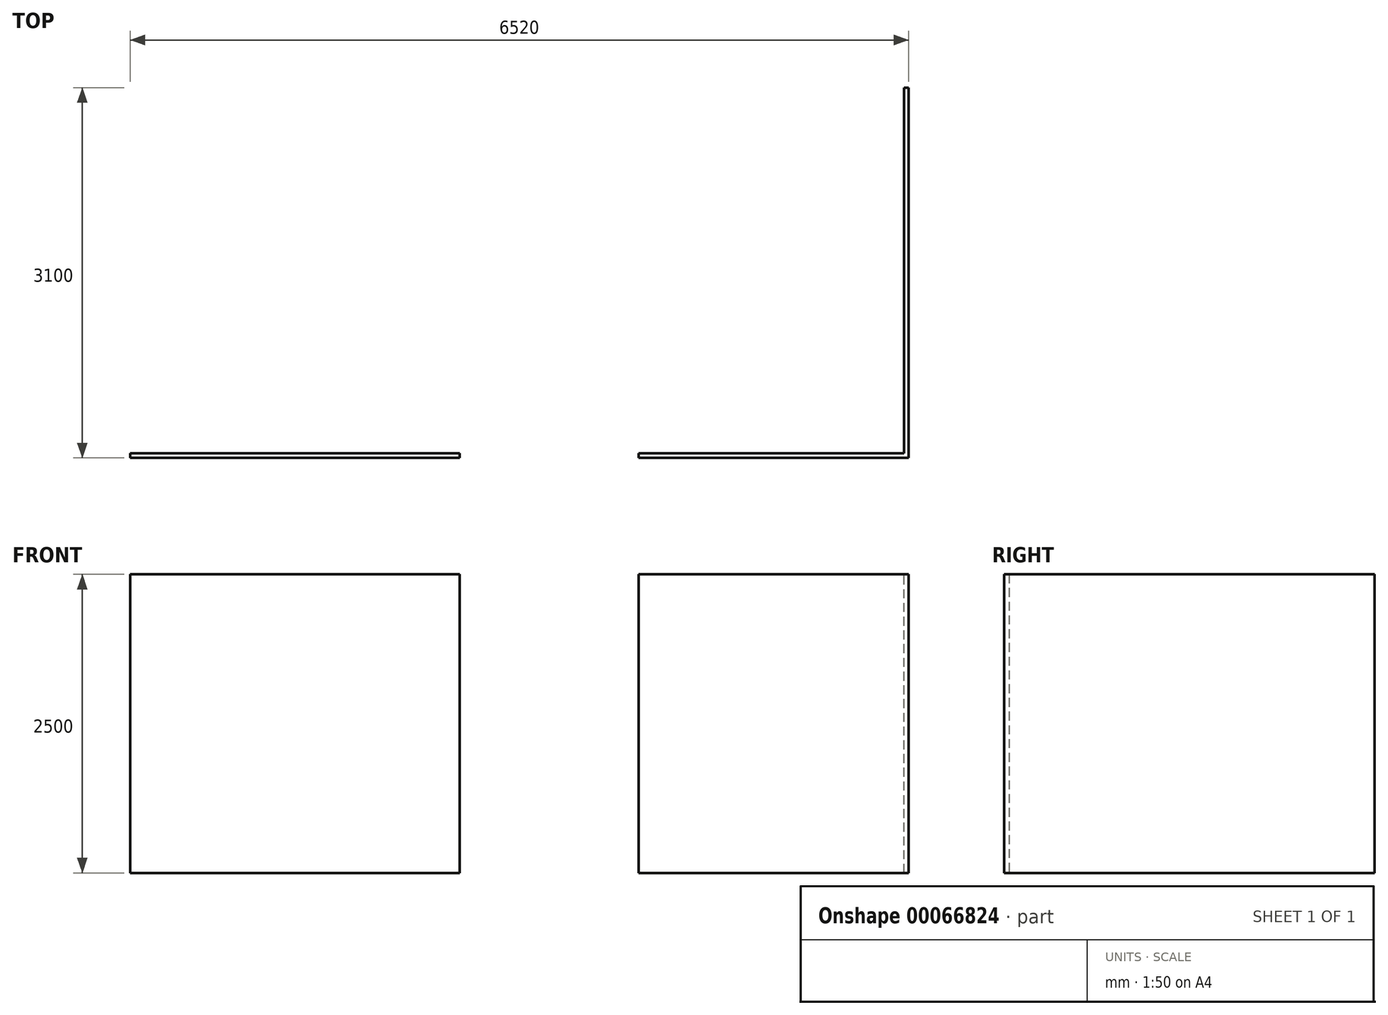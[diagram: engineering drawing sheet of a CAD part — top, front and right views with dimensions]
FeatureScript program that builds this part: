
annotation { "Feature Type Name" : "Feature", "Feature Type Description" : "" }
export const myFeature = defineFeature(function(context is Context, id is Id, definition is map)
    precondition{}
    {
        {
            var Q0;
            Q0=qCreatedBy(makeId("Front.planeOp"),FACE);
            var sketch = newSketch(context, id + "F0", { "sketchPlane" : qUnion([Q0])});
            skLineSegment(sketch, "E0.bottom", {"start": v(-1149.97, 1738.25) * mm, "end": v(1110.03, 1738.25) * mm});
            skLineSegment(sketch, "E0.top", {"start": v(-1149.97, -761.75) * mm, "end": v(1110.03, -761.75) * mm});
            skLineSegment(sketch, "E0.left", {"start": v(-1149.97, 1738.25) * mm, "end": v(-1149.97, -761.75) * mm});
            skLineSegment(sketch, "E0.right", {"start": v(1110.03, 1738.25) * mm, "end": v(1110.03, -761.75) * mm});
            skSolve(sketch);
        }
        {
            var Q0;
            Q0=makeQuery(id+"F0.imprint","IMPRINT",FACE,{"disambiguationData":[TD([[makeQuery(id+"F0.imprint","IMPRINT",EDGE,{"derivedFrom":sQuery(id+"F0.wireOp",EDGE,"E0.bottom")}),-1.0]])]});
            extrude(context, id + "F1", {"entities" : qUnion([Q0]), "depth" : 40 * mm});
        }
        {
            var Q0;
            Q0=makeQuery(id+"F1.opExtrude","SWEPT_FACE",FACE,{"disambiguationData":[OSD([sQuery(id+"F0.wireOp",EDGE,"E0.right")])]});
            var sketch = newSketch(context, id + "F2", { "sketchPlane" : qUnion([Q0])});
            skLineSegment(sketch, "E1.bottom", {"start": v(-40, 1738.25) * mm, "end": v(3060, 1738.25) * mm});
            skLineSegment(sketch, "E1.top", {"start": v(-40, -761.75) * mm, "end": v(3060, -761.75) * mm});
            skLineSegment(sketch, "E1.left", {"start": v(-40, 1738.25) * mm, "end": v(-40, -761.75) * mm});
            skLineSegment(sketch, "E1.right", {"start": v(3060, 1738.25) * mm, "end": v(3060, -761.75) * mm});
            skSolve(sketch);
        }
        {
            var Q0;
            {var subQ2=sQuery(id+"F2.wireOp",EDGE,"E1.left");Q0=makeQuery(id+"F2.imprint","IMPRINT",FACE,{"disambiguationData":[TD([[makeQuery(id+"F2.imprint","IMPRINT",EDGE,{"derivedFrom":subQ2}),1.0]])]});}
            var Q1;
            {var subQ2=sQuery(id+"F2.wireOp",EDGE,"E1.right");Q1=makeQuery(id+"F2.imprint","IMPRINT",FACE,{"disambiguationData":[TD([[makeQuery(id+"F2.imprint","IMPRINT",EDGE,{"derivedFrom":subQ2}),-1.0]])]});}
            extrude(context, id + "F3", {"entities" : qUnion([Q0, Q1]), "operationType" : NewBodyOperationType.ADD, "oppositeDirection" : true, "depth" : 40 * mm});
        }
        {
            var Q0;
            Q0=makeQuery(id+"F1.opExtrude","CAP_FACE",FACE,{"disambiguationData":[OSD([sQuery(id+"F0.wireOp",EDGE,"E0.bottom"),sQuery(id+"F0.wireOp",EDGE,"E0.top"),sQuery(id+"F0.wireOp",EDGE,"E0.left"),sQuery(id+"F0.wireOp",EDGE,"E0.right")])],"isStart":false});
            var sketch = newSketch(context, id + "F4", { "sketchPlane" : qUnion([Q0])});
            skLineSegment(sketch, "E2.bottom", {"start": v(-1149.97, 1738.25) * mm, "end": v(1110.03, 1738.25) * mm});
            skLineSegment(sketch, "E2.top", {"start": v(-1149.97, 1438.25) * mm, "end": v(810.03, 1438.25) * mm});
            skLineSegment(sketch, "E2.left", {"start": v(-1149.97, 1738.25) * mm, "end": v(-1149.97, 1438.25) * mm});
            skLineSegment(sketch, "E2.right", {"start": v(1110.03, 1738.25) * mm, "end": v(1110.03, 1438.25) * mm});
            skLineSegment(sketch, "E3.bottom", {"start": v(1110.03, -761.75) * mm, "end": v(810.03, -761.75) * mm});
            skLineSegment(sketch, "E3.left", {"start": v(1110.03, -761.75) * mm, "end": v(1110.03, 1438.25) * mm});
            skLineSegment(sketch, "E3.right", {"start": v(810.03, -761.75) * mm, "end": v(810.03, 1438.25) * mm});
            skLineSegment(sketch, "E4", {"start": v(750.03, 1438.25) * mm, "end": v(750.03, -761.75) * mm});
            skLineSegment(sketch, "E5", {"start": v(735.03, 1438.25) * mm, "end": v(735.03, -761.75) * mm});
            skLineSegment(sketch, "E6", {"start": v(675.03, 1438.25) * mm, "end": v(675.03, -761.75) * mm});
            skLineSegment(sketch, "E7", {"start": v(660.03, 1438.25) * mm, "end": v(660.03, -761.75) * mm});
            skLineSegment(sketch, "E8", {"start": v(600.03, 1438.25) * mm, "end": v(600.03, -761.75) * mm});
            skLineSegment(sketch, "E9", {"start": v(585.03, 1438.25) * mm, "end": v(585.03, -761.75) * mm});
            skLineSegment(sketch, "E10.1.0.0", {"start": v(360.03, 1438.25) * mm, "end": v(360.03, -761.75) * mm});
            skLineSegment(sketch, "E10.1.0.1", {"start": v(375.03, 1438.25) * mm, "end": v(375.03, -761.75) * mm});
            skLineSegment(sketch, "E10.1.0.2", {"start": v(435.03, 1438.25) * mm, "end": v(435.03, -761.75) * mm});
            skLineSegment(sketch, "E10.1.0.3", {"start": v(450.03, 1438.25) * mm, "end": v(450.03, -761.75) * mm});
            skLineSegment(sketch, "E10.1.0.4", {"start": v(510.03, 1438.25) * mm, "end": v(510.03, -761.75) * mm});
            skLineSegment(sketch, "E10.1.0.5", {"start": v(525.03, 1438.25) * mm, "end": v(525.03, -761.75) * mm});
            skLineSegment(sketch, "E10.2.0.0", {"start": v(135.03, 1438.25) * mm, "end": v(135.03, -761.75) * mm});
            skLineSegment(sketch, "E10.2.0.1", {"start": v(150.03, 1438.25) * mm, "end": v(150.03, -761.75) * mm});
            skLineSegment(sketch, "E10.2.0.2", {"start": v(210.03, 1438.25) * mm, "end": v(210.03, -761.75) * mm});
            skLineSegment(sketch, "E10.2.0.3", {"start": v(225.03, 1438.25) * mm, "end": v(225.03, -761.75) * mm});
            skLineSegment(sketch, "E10.2.0.4", {"start": v(285.03, 1438.25) * mm, "end": v(285.03, -761.75) * mm});
            skLineSegment(sketch, "E10.2.0.5", {"start": v(300.03, 1438.25) * mm, "end": v(300.03, -761.75) * mm});
            skLineSegment(sketch, "E10.3.0.0", {"start": v(-89.97, 1438.25) * mm, "end": v(-89.97, -761.75) * mm});
            skLineSegment(sketch, "E10.3.0.1", {"start": v(-74.97, 1438.25) * mm, "end": v(-74.97, -761.75) * mm});
            skLineSegment(sketch, "E10.3.0.2", {"start": v(-14.97, 1438.25) * mm, "end": v(-14.97, -761.75) * mm});
            skLineSegment(sketch, "E10.3.0.3", {"start": v(0.03, 1438.25) * mm, "end": v(0.03, -761.75) * mm});
            skLineSegment(sketch, "E10.3.0.4", {"start": v(60.03, 1438.25) * mm, "end": v(60.03, -761.75) * mm});
            skLineSegment(sketch, "E10.3.0.5", {"start": v(75.03, 1438.25) * mm, "end": v(75.03, -761.75) * mm});
            skLineSegment(sketch, "E10.4.0.0", {"start": v(-314.97, 1438.25) * mm, "end": v(-314.97, -761.75) * mm});
            skLineSegment(sketch, "E10.4.0.1", {"start": v(-299.97, 1438.25) * mm, "end": v(-299.97, -761.75) * mm});
            skLineSegment(sketch, "E10.4.0.2", {"start": v(-239.97, 1438.25) * mm, "end": v(-239.97, -761.75) * mm});
            skLineSegment(sketch, "E10.4.0.3", {"start": v(-224.97, 1438.25) * mm, "end": v(-224.97, -761.75) * mm});
            skLineSegment(sketch, "E10.4.0.4", {"start": v(-164.97, 1438.25) * mm, "end": v(-164.97, -761.75) * mm});
            skLineSegment(sketch, "E10.4.0.5", {"start": v(-149.97, 1438.25) * mm, "end": v(-149.97, -761.75) * mm});
            skLineSegment(sketch, "E10.5.0.0", {"start": v(-539.97, 1438.25) * mm, "end": v(-539.97, -761.75) * mm});
            skLineSegment(sketch, "E10.5.0.1", {"start": v(-524.97, 1438.25) * mm, "end": v(-524.97, -761.75) * mm});
            skLineSegment(sketch, "E10.5.0.2", {"start": v(-464.97, 1438.25) * mm, "end": v(-464.97, -761.75) * mm});
            skLineSegment(sketch, "E10.5.0.3", {"start": v(-449.97, 1438.25) * mm, "end": v(-449.97, -761.75) * mm});
            skLineSegment(sketch, "E10.5.0.4", {"start": v(-389.97, 1438.25) * mm, "end": v(-389.97, -761.75) * mm});
            skLineSegment(sketch, "E10.5.0.5", {"start": v(-374.97, 1438.25) * mm, "end": v(-374.97, -761.75) * mm});
            skLineSegment(sketch, "E10.6.0.0", {"start": v(-764.97, 1438.25) * mm, "end": v(-764.97, -761.75) * mm});
            skLineSegment(sketch, "E10.6.0.1", {"start": v(-749.97, 1438.25) * mm, "end": v(-749.97, -761.75) * mm});
            skLineSegment(sketch, "E10.6.0.2", {"start": v(-689.97, 1438.25) * mm, "end": v(-689.97, -761.75) * mm});
            skLineSegment(sketch, "E10.6.0.3", {"start": v(-674.97, 1438.25) * mm, "end": v(-674.97, -761.75) * mm});
            skLineSegment(sketch, "E10.6.0.4", {"start": v(-614.97, 1438.25) * mm, "end": v(-614.97, -761.75) * mm});
            skLineSegment(sketch, "E10.6.0.5", {"start": v(-599.97, 1438.25) * mm, "end": v(-599.97, -761.75) * mm});
            skLineSegment(sketch, "E10.7.0.0", {"start": v(-989.97, 1438.25) * mm, "end": v(-989.97, -761.75) * mm});
            skLineSegment(sketch, "E10.7.0.1", {"start": v(-974.97, 1438.25) * mm, "end": v(-974.97, -761.75) * mm});
            skLineSegment(sketch, "E10.7.0.2", {"start": v(-914.97, 1438.25) * mm, "end": v(-914.97, -761.75) * mm});
            skLineSegment(sketch, "E10.7.0.3", {"start": v(-899.97, 1438.25) * mm, "end": v(-899.97, -761.75) * mm});
            skLineSegment(sketch, "E10.7.0.4", {"start": v(-839.97, 1438.25) * mm, "end": v(-839.97, -761.75) * mm});
            skLineSegment(sketch, "E10.7.0.5", {"start": v(-824.97, 1438.25) * mm, "end": v(-824.97, -761.75) * mm});
            skLineSegment(sketch, "E10.8.0.2", {"start": v(-1139.97, 1438.25) * mm, "end": v(-1139.97, -761.75) * mm});
            skLineSegment(sketch, "E10.8.0.3", {"start": v(-1124.97, 1438.25) * mm, "end": v(-1124.97, -761.75) * mm});
            skLineSegment(sketch, "E10.8.0.4", {"start": v(-1064.97, 1438.25) * mm, "end": v(-1064.97, -761.75) * mm});
            skLineSegment(sketch, "E10.8.0.5", {"start": v(-1049.97, 1438.25) * mm, "end": v(-1049.97, -761.75) * mm});
            skLineSegment(sketch, "E10.direction1", {"start": v(585.03, -761.75) * mm, "end": v(360.03, -761.75) * mm, "construction": true});
            skPoint(sketch, "E11.end.orphan", {"position": v(585.03, 996.16) * mm});
            skPoint(sketch, "E12.end.orphan", {"position": v(600.03, 996.16) * mm});
            skPoint(sketch, "E13.end.orphan", {"position": v(660.03, 996.16) * mm});
            skPoint(sketch, "E14.end.orphan", {"position": v(675.03, 996.16) * mm});
            skPoint(sketch, "E15.end.orphan", {"position": v(750.03, 808.78) * mm});
            skPoint(sketch, "E16.end.orphan", {"position": v(735.03, 370.6) * mm});
            skSolve(sketch);
        }
        {
            var Q0;
            Q0=makeQuery(id+"F3.boolean.opBoolean","MERGE",FACE,{"derivedFrom":[makeQuery(id+"F1.opExtrude","SWEPT_FACE",FACE,{"disambiguationData":[OSD([sQuery(id+"F0.wireOp",EDGE,"E0.right")])]}),makeQuery(id+"F3.opExtrude","CAP_FACE",FACE,{"disambiguationData":[OSD([sQuery(id+"F2.wireOp",EDGE,"E1.bottom"),sQuery(id+"F2.wireOp",EDGE,"E1.top"),sQuery(id+"F2.wireOp",EDGE,"E1.left"),sQuery(id+"F2.wireOp",EDGE,"E1.right")])],"isStart":true})]});
            var sketch = newSketch(context, id + "F5", { "sketchPlane" : qUnion([Q0])});
            skLineSegment(sketch, "E17.bottom", {"start": v(-40, 1738.25) * mm, "end": v(3060, 1738.25) * mm});
            skLineSegment(sketch, "E17.top", {"start": v(260, 1438.25) * mm, "end": v(3060, 1438.25) * mm});
            skLineSegment(sketch, "E17.left", {"start": v(-40, 1738.25) * mm, "end": v(-40, 1438.25) * mm});
            skLineSegment(sketch, "E17.right", {"start": v(3060, 1738.25) * mm, "end": v(3060, 1438.25) * mm});
            skLineSegment(sketch, "E18.top", {"start": v(-40, -761.75) * mm, "end": v(260, -761.75) * mm});
            skLineSegment(sketch, "E18.left", {"start": v(-40, 1438.25) * mm, "end": v(-40, -761.75) * mm});
            skLineSegment(sketch, "E18.right", {"start": v(260, 1438.25) * mm, "end": v(260, -761.75) * mm});
            skLineSegment(sketch, "E19", {"start": v(260, 1087.29) * mm, "end": v(320, 1087.29) * mm});
            skLineSegment(sketch, "E20", {"start": v(320, 1438.25) * mm, "end": v(320, -761.75) * mm});
            skLineSegment(sketch, "E21", {"start": v(320, 1087.29) * mm, "end": v(335, 1087.29) * mm});
            skLineSegment(sketch, "E22", {"start": v(335, 1438.25) * mm, "end": v(335, -761.75) * mm});
            skLineSegment(sketch, "E23.1.0.0", {"start": v(395, 1438.25) * mm, "end": v(395, -761.75) * mm});
            skLineSegment(sketch, "E23.1.0.1", {"start": v(410, 1438.25) * mm, "end": v(410, -761.75) * mm});
            skLineSegment(sketch, "E23.1.0.2", {"start": v(335, 1087.29) * mm, "end": v(395, 1087.29) * mm});
            skLineSegment(sketch, "E23.2.0.0", {"start": v(470, 1438.25) * mm, "end": v(470, -761.75) * mm});
            skLineSegment(sketch, "E23.2.0.1", {"start": v(485, 1438.25) * mm, "end": v(485, -761.75) * mm});
            skLineSegment(sketch, "E23.2.0.2", {"start": v(410, 1087.29) * mm, "end": v(470, 1087.29) * mm});
            skLineSegment(sketch, "E23.3.0.0", {"start": v(545, 1438.25) * mm, "end": v(545, -761.75) * mm});
            skLineSegment(sketch, "E23.3.0.1", {"start": v(560, 1438.25) * mm, "end": v(560, -761.75) * mm});
            skLineSegment(sketch, "E23.4.0.0", {"start": v(620, 1438.25) * mm, "end": v(620, -761.75) * mm});
            skLineSegment(sketch, "E23.4.0.1", {"start": v(635, 1438.25) * mm, "end": v(635, -761.75) * mm});
            skLineSegment(sketch, "E23.5.0.0", {"start": v(695, 1438.25) * mm, "end": v(695, -761.75) * mm});
            skLineSegment(sketch, "E23.5.0.1", {"start": v(710, 1438.25) * mm, "end": v(710, -761.75) * mm});
            skLineSegment(sketch, "E23.6.0.0", {"start": v(770, 1438.25) * mm, "end": v(770, -761.75) * mm});
            skLineSegment(sketch, "E23.6.0.1", {"start": v(785, 1438.25) * mm, "end": v(785, -761.75) * mm});
            skLineSegment(sketch, "E23.7.0.0", {"start": v(845, 1438.25) * mm, "end": v(845, -761.75) * mm});
            skLineSegment(sketch, "E23.7.0.1", {"start": v(860, 1438.25) * mm, "end": v(860, -761.75) * mm});
            skLineSegment(sketch, "E23.8.0.0", {"start": v(920, 1438.25) * mm, "end": v(920, -761.75) * mm});
            skLineSegment(sketch, "E23.8.0.1", {"start": v(935, 1438.25) * mm, "end": v(935, -761.75) * mm});
            skLineSegment(sketch, "E23.9.0.0", {"start": v(995, 1438.25) * mm, "end": v(995, -761.75) * mm});
            skLineSegment(sketch, "E23.9.0.1", {"start": v(1010, 1438.25) * mm, "end": v(1010, -761.75) * mm});
            skLineSegment(sketch, "E23.10.0.0", {"start": v(1070, 1438.25) * mm, "end": v(1070, -761.75) * mm});
            skLineSegment(sketch, "E23.10.0.1", {"start": v(1085, 1438.25) * mm, "end": v(1085, -761.75) * mm});
            skLineSegment(sketch, "E23.11.0.0", {"start": v(1145, 1438.25) * mm, "end": v(1145, -761.75) * mm});
            skLineSegment(sketch, "E23.11.0.1", {"start": v(1160, 1438.25) * mm, "end": v(1160, -761.75) * mm});
            skLineSegment(sketch, "E23.12.0.0", {"start": v(1220, 1438.25) * mm, "end": v(1220, -761.75) * mm});
            skLineSegment(sketch, "E23.12.0.1", {"start": v(1235, 1438.25) * mm, "end": v(1235, -761.75) * mm});
            skLineSegment(sketch, "E23.13.0.0", {"start": v(1295, 1438.25) * mm, "end": v(1295, -761.75) * mm});
            skLineSegment(sketch, "E23.13.0.1", {"start": v(1310, 1438.25) * mm, "end": v(1310, -761.75) * mm});
            skLineSegment(sketch, "E23.14.0.0", {"start": v(1370, 1438.25) * mm, "end": v(1370, -761.75) * mm});
            skLineSegment(sketch, "E23.14.0.1", {"start": v(1385, 1438.25) * mm, "end": v(1385, -761.75) * mm});
            skLineSegment(sketch, "E23.15.0.0", {"start": v(1445, 1438.25) * mm, "end": v(1445, -761.75) * mm});
            skLineSegment(sketch, "E23.15.0.1", {"start": v(1460, 1438.25) * mm, "end": v(1460, -761.75) * mm});
            skLineSegment(sketch, "E23.16.0.0", {"start": v(1520, 1438.25) * mm, "end": v(1520, -761.75) * mm});
            skLineSegment(sketch, "E23.16.0.1", {"start": v(1535, 1438.25) * mm, "end": v(1535, -761.75) * mm});
            skLineSegment(sketch, "E23.17.0.0", {"start": v(1595, 1438.25) * mm, "end": v(1595, -761.75) * mm});
            skLineSegment(sketch, "E23.17.0.1", {"start": v(1610, 1438.25) * mm, "end": v(1610, -761.75) * mm});
            skLineSegment(sketch, "E23.18.0.0", {"start": v(1670, 1438.25) * mm, "end": v(1670, -761.75) * mm});
            skLineSegment(sketch, "E23.18.0.1", {"start": v(1685, 1438.25) * mm, "end": v(1685, -761.75) * mm});
            skLineSegment(sketch, "E23.19.0.0", {"start": v(1745, 1438.25) * mm, "end": v(1745, -761.75) * mm});
            skLineSegment(sketch, "E23.19.0.1", {"start": v(1760, 1438.25) * mm, "end": v(1760, -761.75) * mm});
            skLineSegment(sketch, "E23.20.0.0", {"start": v(1820, 1438.25) * mm, "end": v(1820, -761.75) * mm});
            skLineSegment(sketch, "E23.20.0.1", {"start": v(1835, 1438.25) * mm, "end": v(1835, -761.75) * mm});
            skLineSegment(sketch, "E23.21.0.0", {"start": v(1895, 1438.25) * mm, "end": v(1895, -761.75) * mm});
            skLineSegment(sketch, "E23.21.0.1", {"start": v(1910, 1438.25) * mm, "end": v(1910, -761.75) * mm});
            skLineSegment(sketch, "E23.22.0.0", {"start": v(1970, 1438.25) * mm, "end": v(1970, -761.75) * mm});
            skLineSegment(sketch, "E23.22.0.1", {"start": v(1985, 1438.25) * mm, "end": v(1985, -761.75) * mm});
            skLineSegment(sketch, "E23.23.0.0", {"start": v(2045, 1438.25) * mm, "end": v(2045, -761.75) * mm});
            skLineSegment(sketch, "E23.23.0.1", {"start": v(2060, 1438.25) * mm, "end": v(2060, -761.75) * mm});
            skLineSegment(sketch, "E23.24.0.0", {"start": v(2120, 1438.25) * mm, "end": v(2120, -761.75) * mm});
            skLineSegment(sketch, "E23.24.0.1", {"start": v(2135, 1438.25) * mm, "end": v(2135, -761.75) * mm});
            skLineSegment(sketch, "E23.25.0.0", {"start": v(2195, 1438.25) * mm, "end": v(2195, -761.75) * mm});
            skLineSegment(sketch, "E23.25.0.1", {"start": v(2210, 1438.25) * mm, "end": v(2210, -761.75) * mm});
            skLineSegment(sketch, "E23.26.0.0", {"start": v(2270, 1438.25) * mm, "end": v(2270, -761.75) * mm});
            skLineSegment(sketch, "E23.26.0.1", {"start": v(2285, 1438.25) * mm, "end": v(2285, -761.75) * mm});
            skLineSegment(sketch, "E23.27.0.0", {"start": v(2345, 1438.25) * mm, "end": v(2345, -761.75) * mm});
            skLineSegment(sketch, "E23.27.0.1", {"start": v(2360, 1438.25) * mm, "end": v(2360, -761.75) * mm});
            skLineSegment(sketch, "E23.28.0.0", {"start": v(2420, 1438.25) * mm, "end": v(2420, -761.75) * mm});
            skLineSegment(sketch, "E23.28.0.1", {"start": v(2435, 1438.25) * mm, "end": v(2435, -761.75) * mm});
            skLineSegment(sketch, "E23.29.0.0", {"start": v(2495, 1438.25) * mm, "end": v(2495, -761.75) * mm});
            skLineSegment(sketch, "E23.29.0.1", {"start": v(2510, 1438.25) * mm, "end": v(2510, -761.75) * mm});
            skLineSegment(sketch, "E23.30.0.0", {"start": v(2570, 1438.25) * mm, "end": v(2570, -761.75) * mm});
            skLineSegment(sketch, "E23.30.0.1", {"start": v(2585, 1438.25) * mm, "end": v(2585, -761.75) * mm});
            skLineSegment(sketch, "E23.31.0.0", {"start": v(2645, 1438.25) * mm, "end": v(2645, -761.75) * mm});
            skLineSegment(sketch, "E23.31.0.1", {"start": v(2660, 1438.25) * mm, "end": v(2660, -761.75) * mm});
            skLineSegment(sketch, "E23.32.0.0", {"start": v(2720, 1438.25) * mm, "end": v(2720, -761.75) * mm});
            skLineSegment(sketch, "E23.32.0.1", {"start": v(2735, 1438.25) * mm, "end": v(2735, -761.75) * mm});
            skLineSegment(sketch, "E23.33.0.0", {"start": v(2795, 1438.25) * mm, "end": v(2795, -761.75) * mm});
            skLineSegment(sketch, "E23.33.0.1", {"start": v(2810, 1438.25) * mm, "end": v(2810, -761.75) * mm});
            skLineSegment(sketch, "E23.34.0.0", {"start": v(2870, 1438.25) * mm, "end": v(2870, -761.75) * mm});
            skLineSegment(sketch, "E23.34.0.1", {"start": v(2885, 1438.25) * mm, "end": v(2885, -761.75) * mm});
            skLineSegment(sketch, "E23.35.0.0", {"start": v(2945, 1438.25) * mm, "end": v(2945, -761.75) * mm});
            skLineSegment(sketch, "E23.35.0.1", {"start": v(2960, 1438.25) * mm, "end": v(2960, -761.75) * mm});
            skLineSegment(sketch, "E23.36.0.0", {"start": v(3020, 1438.25) * mm, "end": v(3020, -761.75) * mm});
            skLineSegment(sketch, "E23.36.0.1", {"start": v(3035, 1438.25) * mm, "end": v(3035, -761.75) * mm});
            skLineSegment(sketch, "E23.direction1", {"start": v(320, -761.75) * mm, "end": v(395, -761.75) * mm, "construction": true});
            skPoint(sketch, "E24.orphan", {"position": v(3110, 1438.25) * mm});
            skPoint(sketch, "E25.orphan", {"position": v(3185, -761.75) * mm});
            skSolve(sketch);
        }
        {
            var Q0;
            Q0=makeQuery(id+"F4.imprint","IMPRINT",FACE,{"disambiguationData":[TD([[makeQuery(id+"F4.imprint","IMPRINT",EDGE,{"derivedFrom":sQuery(id+"F4.wireOp",EDGE,"E2.bottom")}),-1.0]])]});
            var sketch = newSketch(context, id + "F6", { "sketchPlane" : qUnion([Q0])});
            skLineSegment(sketch, "E26.0", {"start": v(-1149.97, -761.75) * mm, "end": v(1110.03, -761.75) * mm});
            skLineSegment(sketch, "E27", {"start": v(256, -761.75) * mm, "end": v(256, -261.75) * mm});
            skLineSegment(sketch, "E28.bottom", {"start": v(809.56, 1238.25) * mm, "end": v(-403.32, 1238.25) * mm});
            skLineSegment(sketch, "E28.top", {"start": v(809.56, -261.75) * mm, "end": v(-403.32, -261.75) * mm});
            skLineSegment(sketch, "E28.left", {"start": v(809.56, 1238.25) * mm, "end": v(809.56, -261.75) * mm});
            skLineSegment(sketch, "E28.right", {"start": v(-403.32, 1238.25) * mm, "end": v(-403.32, -261.75) * mm});
            skLineSegment(sketch, "E29.0", {"start": v(769.56, 1198.25) * mm, "end": v(-363.32, 1198.25) * mm});
            skLineSegment(sketch, "E29.1", {"start": v(769.56, 1198.25) * mm, "end": v(769.56, -221.75) * mm});
            skLineSegment(sketch, "E29.2", {"start": v(769.56, -221.75) * mm, "end": v(-363.32, -221.75) * mm});
            skLineSegment(sketch, "E29.3", {"start": v(-363.32, 1198.25) * mm, "end": v(-363.32, -221.75) * mm});
            skLineSegment(sketch, "E30.0", {"start": v(1110.03, 1438.25) * mm, "end": v(1110.03, -761.75) * mm});
            skLineSegment(sketch, "E31", {"start": v(810.03, 1438.25) * mm, "end": v(-1149.97, 1438.25) * mm});
            skPoint(sketch, "E32.0.end.orphan", {"position": v(1110.03, 1738.25) * mm});
            skPoint(sketch, "E32.0.start.orphan", {"position": v(-1149.97, 1738.25) * mm});
            skPoint(sketch, "E33.end.orphan", {"position": v(260.48, 1238.25) * mm});
            skLineSegment(sketch, "E34.0", {"start": v(-1149.97, 1738.25) * mm, "end": v(-1149.97, -761.75) * mm});
            skLineSegment(sketch, "E35", {"start": v(-403.32, 1238.25) * mm, "end": v(-1149.97, 1238.25) * mm});
            skSolve(sketch);
        }
        {
            var Q0;
            Q0=makeQuery(id+"F4.imprint","IMPRINT",FACE,{"disambiguationData":[TD([[makeQuery(id+"F4.imprint","IMPRINT",EDGE,{"derivedFrom":sQuery(id+"F4.wireOp",EDGE,"E2.bottom")}),-1.0]])]});
            var sketch = newSketch(context, id + "F7", { "sketchPlane" : qUnion([Q0])});
            skLineSegment(sketch, "E36.0", {"start": v(-1149.97, 1738.25) * mm, "end": v(-1149.97, -761.75) * mm});
            skLineSegment(sketch, "E37.bottom", {"start": v(-2649.97, 1738.25) * mm, "end": v(-5409.97, 1738.25) * mm});
            skLineSegment(sketch, "E37.top", {"start": v(-2649.97, -761.75) * mm, "end": v(-5409.97, -761.75) * mm});
            skLineSegment(sketch, "E37.left", {"start": v(-2649.97, 1738.25) * mm, "end": v(-2649.97, -761.75) * mm});
            skLineSegment(sketch, "E37.right", {"start": v(-5409.97, 1738.25) * mm, "end": v(-5409.97, -761.75) * mm});
            skLineSegment(sketch, "E38", {"start": v(-1149.97, -761.75) * mm, "end": v(-2649.97, -761.75) * mm});
            skSolve(sketch);
        }
        {
            var Q0;
            Q0 = qSketchRegion(id + "F7", true);
            extrude(context, id + "F8", {"entities" : qUnion([Q0]), "oppositeDirection" : true, "depth" : 40 * mm});
        }
    });
